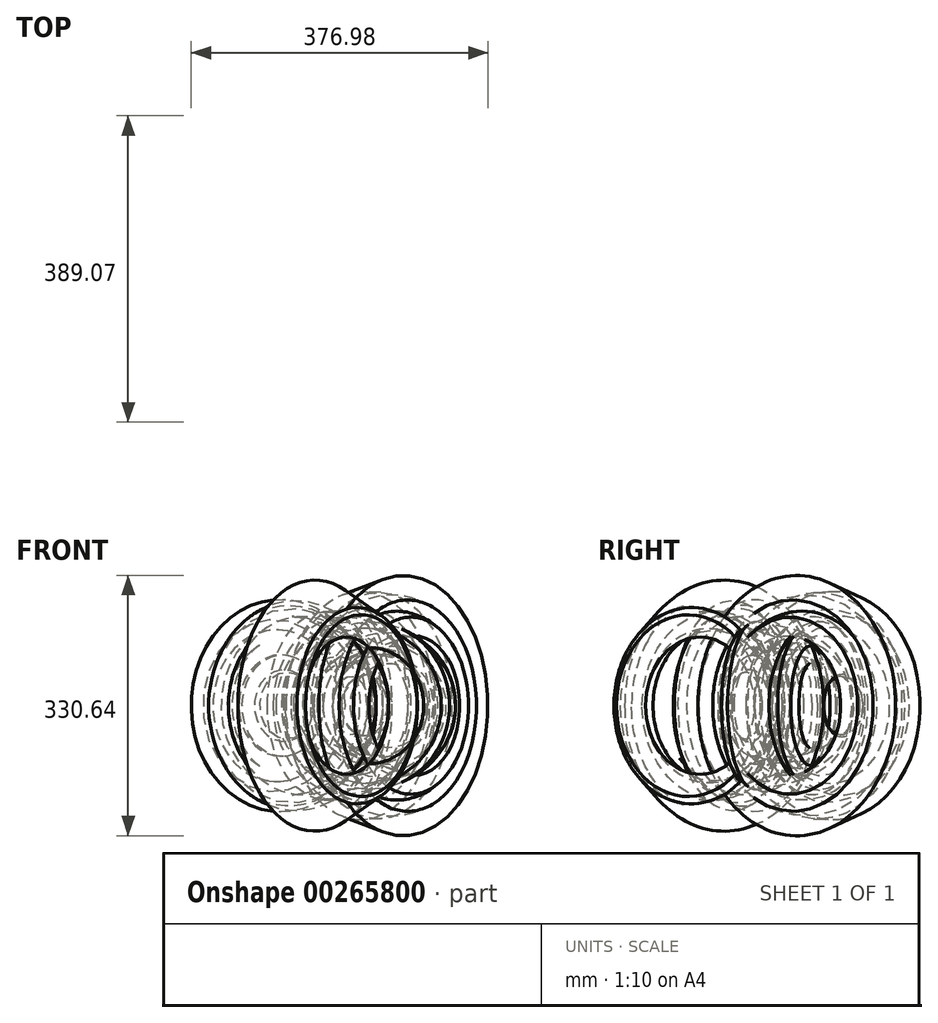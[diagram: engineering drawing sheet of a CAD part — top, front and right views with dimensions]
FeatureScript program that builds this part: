
annotation { "Feature Type Name" : "Feature", "Feature Type Description" : "" }
export const myFeature = defineFeature(function(context is Context, id is Id, definition is map)
    precondition{}
    {
        {
            var Q0;
            Q0=qCreatedBy(makeId("Top.planeOp"),FACE);
            var sketch = newSketch(context, id + "F0", { "sketchPlane" : qUnion([Q0])});
            skFitSpline(sketch, "E0", {"points": [v(-45.64, 48.54) * mm, v(-64.56, -13.43) * mm, v(18.16, -4.27) * mm, v(7.48, -61.97) * mm, v(-43.5, -47.62) * mm, v(-16.94, -34.8) * mm, v(-58.46, -27.47) * mm, v(-64.56, -60.14) * mm, v(48.08, -66.55) * mm, v(65.17, 46.7) * mm, v(67.92, 53.12) * mm, v(29.76, 62.58) * mm, v(38.92, 25.34) * mm, v(52.66, 7.02) * mm, v(45.94, 7.02) * mm, v(34.95, 10.99) * mm, v(30.98, 14.35) * mm, v(7.78, 30.83) * mm, v(5.95, 36.94) * mm, v(0, 54.03) * mm, v(-32.2, 46.4) * mm, v(-33.43, 36.33) * mm, v(0, 14.35) * mm, v(-8.7, 32.66) * mm, v(7.78, 23.81) * mm, v(9, 17.7) * mm, v(10.53, 10.68) * mm, v(-3.82, 2.75) * mm, v(-24.27, 9.77) * mm, v(-43.2, 19.84) * mm, v(-49.3, 5.5) * mm, v(-56.02, 16.48) * mm, v(-45.03, 28.39) * mm, v(-42.9, 35.41) * mm, v(-37.09, 52.2) * mm, v(-22.13, 61.36) * mm, v(-23.96, 69.6) * mm, v(-38.92, 71.43) * mm, v(-49.6, 71.43) * mm, v(-61.51, 67.16) * mm, v(-108.22, -20.15) * mm, v(-45.64, 58.61) * mm, v(-45.64, 48.54) * mm]});
            skLineSegment(sketch, "E1", {"start": v(-102.1, -34.5) * mm, "end": v(-78.9, -52.5) * mm});
            skLineSegment(sketch, "E2", {"start": v(-78.9, -52.5) * mm, "end": v(-107.3, 54.04) * mm});
            skLineSegment(sketch, "E3", {"start": v(-107.3, 54.04) * mm, "end": v(-11.9, 79.45) * mm});
            skLineSegment(sketch, "E4", {"start": v(-11.9, 79.45) * mm, "end": v(28.35, 45.03) * mm});
            skLineSegment(sketch, "E5", {"start": v(28.35, 45.03) * mm, "end": v(2.29, -30.22) * mm});
            skLineSegment(sketch, "E6", {"start": v(2.29, -30.22) * mm, "end": v(69.14, -16.18) * mm});
            skLineSegment(sketch, "E7", {"start": v(69.14, -16.18) * mm, "end": v(27.32, 72.96) * mm});
            skLineSegment(sketch, "E8", {"start": v(27.32, 72.96) * mm, "end": v(-17.86, 62.27) * mm});
            skLineSegment(sketch, "E9", {"start": v(-17.86, 62.27) * mm, "end": v(-80.74, -23.81) * mm});
            skLineSegment(sketch, "E10", {"start": v(-80.74, -23.81) * mm, "end": v(-15.11, -23.81) * mm});
            skLineSegment(sketch, "E11", {"start": v(-15.11, -23.81) * mm, "end": v(2.6, -49.76) * mm});
            skLineSegment(sketch, "E12", {"start": v(2.6, -49.76) * mm, "end": v(-60.9, -96.16) * mm});
            skLineSegment(sketch, "E13", {"start": v(-60.9, -96.16) * mm, "end": v(-102.1, -34.5) * mm});
            skSolve(sketch);
        }
        {
            var Q0;
            {var subQ0=sQuery(id+"F0.wireOp",EDGE,"E5");var subQ1=sQuery(id+"F0.wireOp",EDGE,"E0");var subQ2=makeQuery(id+"F0.imprint","INTERSECT",VERTEX,{"disambiguationData":[OD(0.0)],"derivedFrom":[subQ1,subQ0]});Q0=makeQuery(id+"F0.imprint","IMPRINT",FACE,{"disambiguationData":[TD([[makeQuery(id+"F0.imprint","IMPRINT",EDGE,{"disambiguationData":[TD([[subQ2,1.0]])],"derivedFrom":subQ1}),1.0]])]});}
            var Q1;
            Q1=sQuery(id+"F0.wireOp",EDGE,"E13");
            revolve(context, id + "F1", {"entities" : qUnion([Q0]), "axis" : qUnion([Q1]), "revolveType" : RevolveType.FULL});
        }
        {
            var Q0;
            {var subQ0=sQuery(id+"F0.wireOp",EDGE,"E6");var subQ1=sQuery(id+"F0.wireOp",EDGE,"E0");var subQ2=makeQuery(id+"F0.imprint","INTERSECT",VERTEX,{"disambiguationData":[OD(1.0)],"derivedFrom":[subQ1,subQ0]});Q0=makeQuery(id+"F0.imprint","IMPRINT",FACE,{"disambiguationData":[TD([[makeQuery(id+"F0.imprint","IMPRINT",EDGE,{"disambiguationData":[TD([[subQ2,-1.0]])],"derivedFrom":subQ1}),1.0]])]});}
            var Q1;
            Q1=sQuery(id+"F0.wireOp",EDGE,"E1");
            revolve(context, id + "F2", {"entities" : qUnion([Q0]), "axis" : qUnion([Q1]), "revolveType" : RevolveType.FULL});
        }
        {
            var Q0;
            {var subQ1=sQuery(id+"F0.wireOp",EDGE,"E0");var subQ6=sQuery(id+"F0.wireOp",EDGE,"E3");var subQ7=makeQuery(id+"F0.imprint","INTERSECT",VERTEX,{"disambiguationData":[OD(0.0)],"derivedFrom":[subQ1,subQ6]});Q0=makeQuery(id+"F0.imprint","IMPRINT",FACE,{"disambiguationData":[TD([[makeQuery(id+"F0.imprint","IMPRINT",EDGE,{"disambiguationData":[TD([[subQ7,1.0]])],"derivedFrom":subQ1}),1.0]])]});}
            var Q1;
            Q1=sQuery(id+"F0.wireOp",EDGE,"E5");
            revolve(context, id + "F3", {"entities" : qUnion([Q0]), "axis" : qUnion([Q1]), "revolveType" : RevolveType.FULL});
        }
        {
            var Q0;
            {var subQ0=sQuery(id+"F0.wireOp",EDGE,"E5");var subQ1=sQuery(id+"F0.wireOp",EDGE,"E0");var subQ4=makeQuery(id+"F0.imprint","INTERSECT",VERTEX,{"disambiguationData":[OD(0.0)],"derivedFrom":[subQ1,subQ0]});Q0=makeQuery(id+"F0.imprint","IMPRINT",FACE,{"disambiguationData":[TD([[makeQuery(id+"F0.imprint","IMPRINT",EDGE,{"disambiguationData":[TD([[subQ4,-1.0]])],"derivedFrom":subQ1}),1.0]])]});}
            var Q1;
            Q1=sQuery(id+"F0.wireOp",EDGE,"E9");
            revolve(context, id + "F4", {"entities" : qUnion([Q0]), "axis" : qUnion([Q1]), "revolveType" : RevolveType.FULL});
        }
        {
            var Q0;
            {var subQ1=sQuery(id+"F0.wireOp",EDGE,"E1");Q0=makeQuery(id+"F0.imprint","IMPRINT",FACE,{"disambiguationData":[TD([[makeQuery(id+"F0.imprint","IMPRINT",EDGE,{"derivedFrom":subQ1}),-1.0]])]});}
            var Q1;
            Q1=sQuery(id+"F0.wireOp",EDGE,"E4");
            revolve(context, id + "F5", {"entities" : qUnion([Q0]), "axis" : qUnion([Q1]), "revolveType" : RevolveType.FULL});
        }
    });
